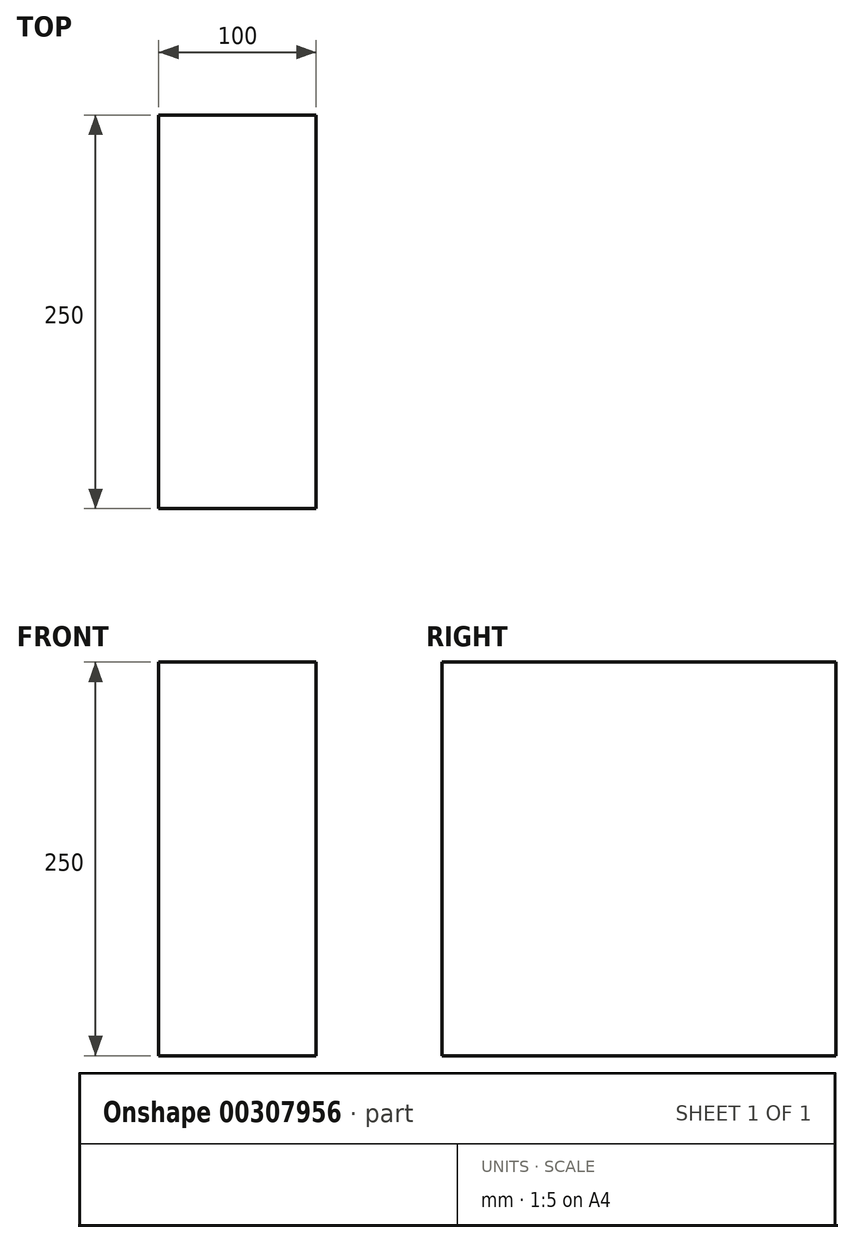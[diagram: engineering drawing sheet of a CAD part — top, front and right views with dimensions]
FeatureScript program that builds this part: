
annotation { "Feature Type Name" : "Feature", "Feature Type Description" : "" }
export const myFeature = defineFeature(function(context is Context, id is Id, definition is map)
    precondition{}
    {
        {
            var Q0;
            Q0=qCreatedBy(makeId("Right.planeOp"),FACE);
            var sketch = newSketch(context, id + "F0", { "sketchPlane" : qUnion([Q0])});
            skLineSegment(sketch, "E0.bottom", {"start": v(-12.45, -6.13) * mm, "end": v(237.55, -6.13) * mm});
            skLineSegment(sketch, "E0.top", {"start": v(-12.45, -256.13) * mm, "end": v(237.55, -256.13) * mm});
            skLineSegment(sketch, "E0.left", {"start": v(-12.45, -6.13) * mm, "end": v(-12.45, -256.13) * mm});
            skLineSegment(sketch, "E0.right", {"start": v(237.55, -6.13) * mm, "end": v(237.55, -256.13) * mm});
            skSolve(sketch);
        }
        {
            var Q0;
            Q0=makeQuery(id+"F0.imprint","IMPRINT",FACE,{"disambiguationData":[TD([[makeQuery(id+"F0.imprint","IMPRINT",EDGE,{"derivedFrom":sQuery(id+"F0.wireOp",EDGE,"E0.bottom")}),-1.0]])]});
            extrude(context, id + "F1", {"entities" : qUnion([Q0]), "depth" : 100 * mm});
        }
    });
